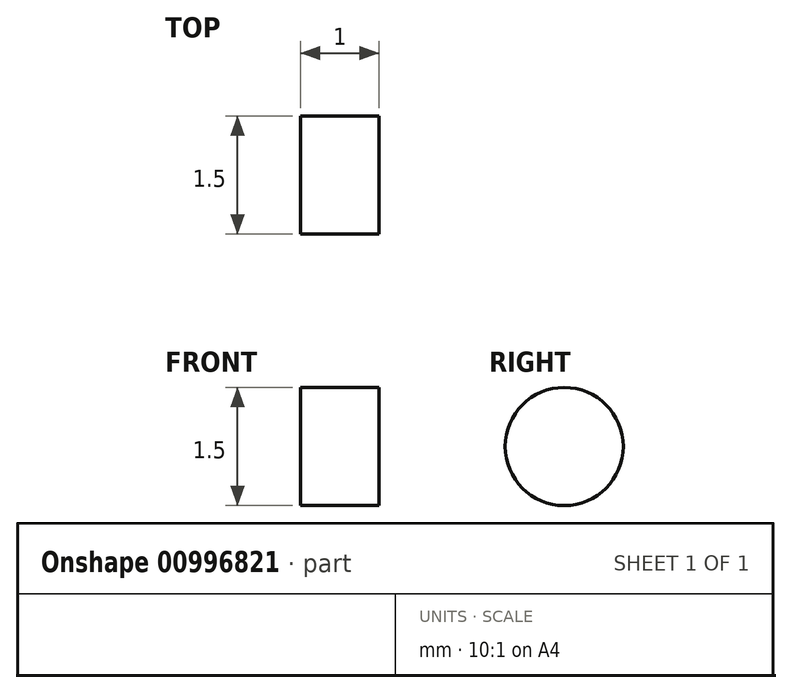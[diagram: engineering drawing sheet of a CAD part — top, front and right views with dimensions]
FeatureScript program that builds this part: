
annotation { "Feature Type Name" : "Feature", "Feature Type Description" : "" }
export const myFeature = defineFeature(function(context is Context, id is Id, definition is map)
    precondition{}
    {
        {
            var Q0;
            Q0=qCreatedBy(makeId("Right.planeOp"),FACE);
            var sketch = newSketch(context, id + "F0", { "sketchPlane" : qUnion([Q0])});
            skCircle(sketch, "E0", {"center": v(0, 0) * mm, "radius": 0.75 * mm});
            skSolve(sketch);
        }
        {
            var Q0;
            Q0 = qSketchRegion(id + "F0", true);
            extrude(context, id + "F1", {"entities" : qUnion([Q0]), "depth" : 1 * mm, "offsetDistance" : 25 * mm});
        }
    });
